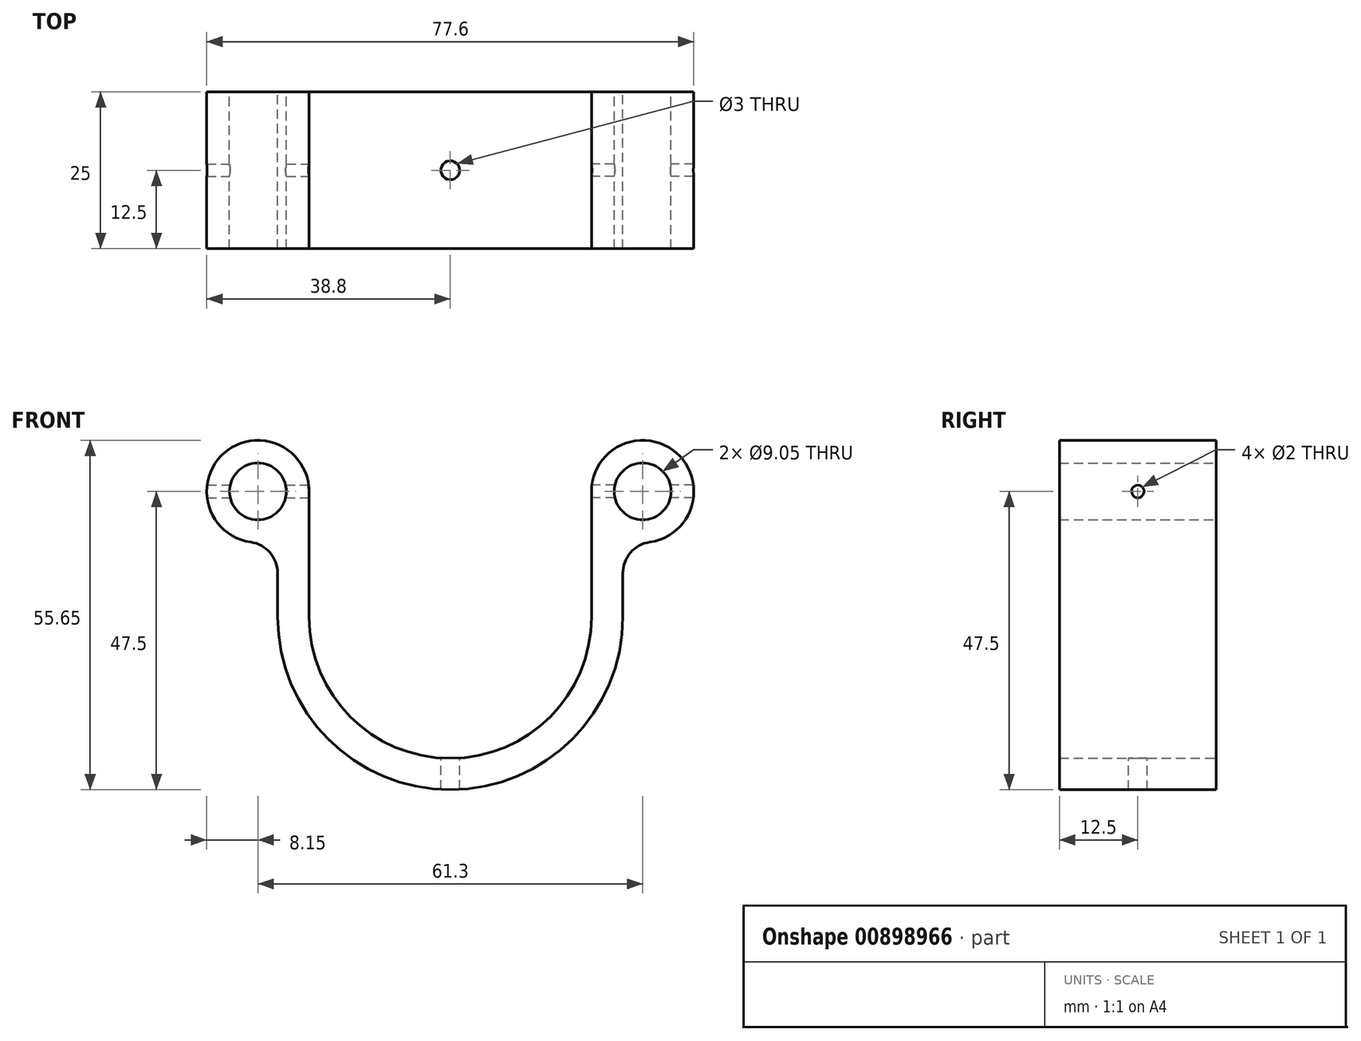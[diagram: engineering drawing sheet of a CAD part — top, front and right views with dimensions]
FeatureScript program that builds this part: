
annotation { "Feature Type Name" : "Feature", "Feature Type Description" : "" }
export const myFeature = defineFeature(function(context is Context, id is Id, definition is map)
    precondition{}
    {
        {
            var Q0;
            Q0=qCreatedBy(makeId("Front.planeOp"),FACE);
            var sketch = newSketch(context, id + "F0", { "sketchPlane" : qUnion([Q0]), "disableImprinting" : false});
            skLineSegment(sketch, "E0", {"start": v(-22.5, 0) * mm, "end": v(-22.5, -20) * mm});
            skLineSegment(sketch, "E1.MirrorCS", {"start": v(22.5, 0) * mm, "end": v(22.5, -20) * mm});
            skArc(sketch, "E2", {"start": v(-22.5, -20) * mm, "mid": v(0, -42.5) * mm, "end": v(22.5, -20) * mm});
            skCircle(sketch, "E3", {"center": v(-30.65, 0) * mm, "radius": 4.53 * mm});
            skArc(sketch, "E4.0", {"start": v(-27.5, -20) * mm, "mid": v(0, -47.5) * mm, "end": v(27.5, -20) * mm});
            skArc(sketch, "E5", {"start": v(-22.5, 0) * mm, "mid": v(-36, 6.15) * mm, "end": v(-31.8, -8.07) * mm});
            skLineSegment(sketch, "E6", {"start": v(-27.5, -20) * mm, "end": v(-27.5, -13.02) * mm});
            skPoint(sketch, "E7.visualSharp", {"position": v(-27.5, -7.52) * mm});
            skArc(sketch, "E7.filletArc", {"start": v(-27.5, -13.02) * mm, "mid": v(-28.72, -9.74) * mm, "end": v(-31.8, -8.07) * mm});
            skCircle(sketch, "E8.MirrorC", {"center": v(30.65, 0) * mm, "radius": 4.53 * mm});
            skArc(sketch, "E9.MirrorCS", {"start": v(22.5, 0) * mm, "mid": v(36, 6.15) * mm, "end": v(31.8, -8.07) * mm});
            skArc(sketch, "E10.MirrorCS", {"start": v(27.5, -13.02) * mm, "mid": v(28.72, -9.74) * mm, "end": v(31.8, -8.07) * mm});
            skLineSegment(sketch, "E11.MirrorCS", {"start": v(27.5, -20) * mm, "end": v(27.5, -13.02) * mm});
            skSolve(sketch);
        }
        {
            var Q0;
            Q0=makeQuery(id+"F0.imprint","IMPRINT",FACE,{"disambiguationData":[TD([[makeQuery(id+"F0.imprint","IMPRINT",EDGE,{"derivedFrom":sQuery(id+"F0.wireOp",EDGE,"E0")}),-1.0]])]});
            extrude(context, id + "F1", {"entities" : qUnion([Q0]), "depth" : 25 * mm, "offsetDistance" : 25 * mm});
        }
        {
            var Q0;
            Q0=qCreatedBy(makeId("Top.planeOp"),FACE);
            var sketch = newSketch(context, id + "F2", { "sketchPlane" : qUnion([Q0])});
            skCircle(sketch, "E12", {"center": v(0, -12.5) * mm, "radius": 1.5 * mm});
            skSolve(sketch);
        }
        {
            var Q0;
            Q0=qSketchRegion(id+"F2",true);
            extrude(context, id + "F3", {"entities" : qUnion([Q0]), "operationType" : NewBodyOperationType.REMOVE, "endBound" : BoundingType.THROUGH_ALL, "oppositeDirection" : true, "depth" : 25 * mm, "offsetDistance" : 25 * mm});
        }
        {
            var Q0;
            Q0=qCreatedBy(makeId("Right.planeOp"),FACE);
            var sketch = newSketch(context, id + "F4", { "sketchPlane" : qUnion([Q0])});
            skCircle(sketch, "E13", {"center": v(-12.5, 0) * mm, "radius": 1 * mm});
            skSolve(sketch);
        }
        {
            var Q0;
            Q0=qSketchRegion(id+"F4",true);
            extrude(context, id + "F5", {"entities" : qUnion([Q0]), "operationType" : NewBodyOperationType.REMOVE, "endBound" : BoundingType.THROUGH_ALL, "depth" : 60 * mm, "offsetDistance" : 25 * mm});
        }
        {
            var Q0;
            Q0=qSketchRegion(id+"F4",true);
            extrude(context, id + "F6", {"entities" : qUnion([Q0]), "operationType" : NewBodyOperationType.REMOVE, "endBound" : BoundingType.THROUGH_ALL, "oppositeDirection" : true, "depth" : 25 * mm, "offsetDistance" : 25 * mm});
        }
    });
